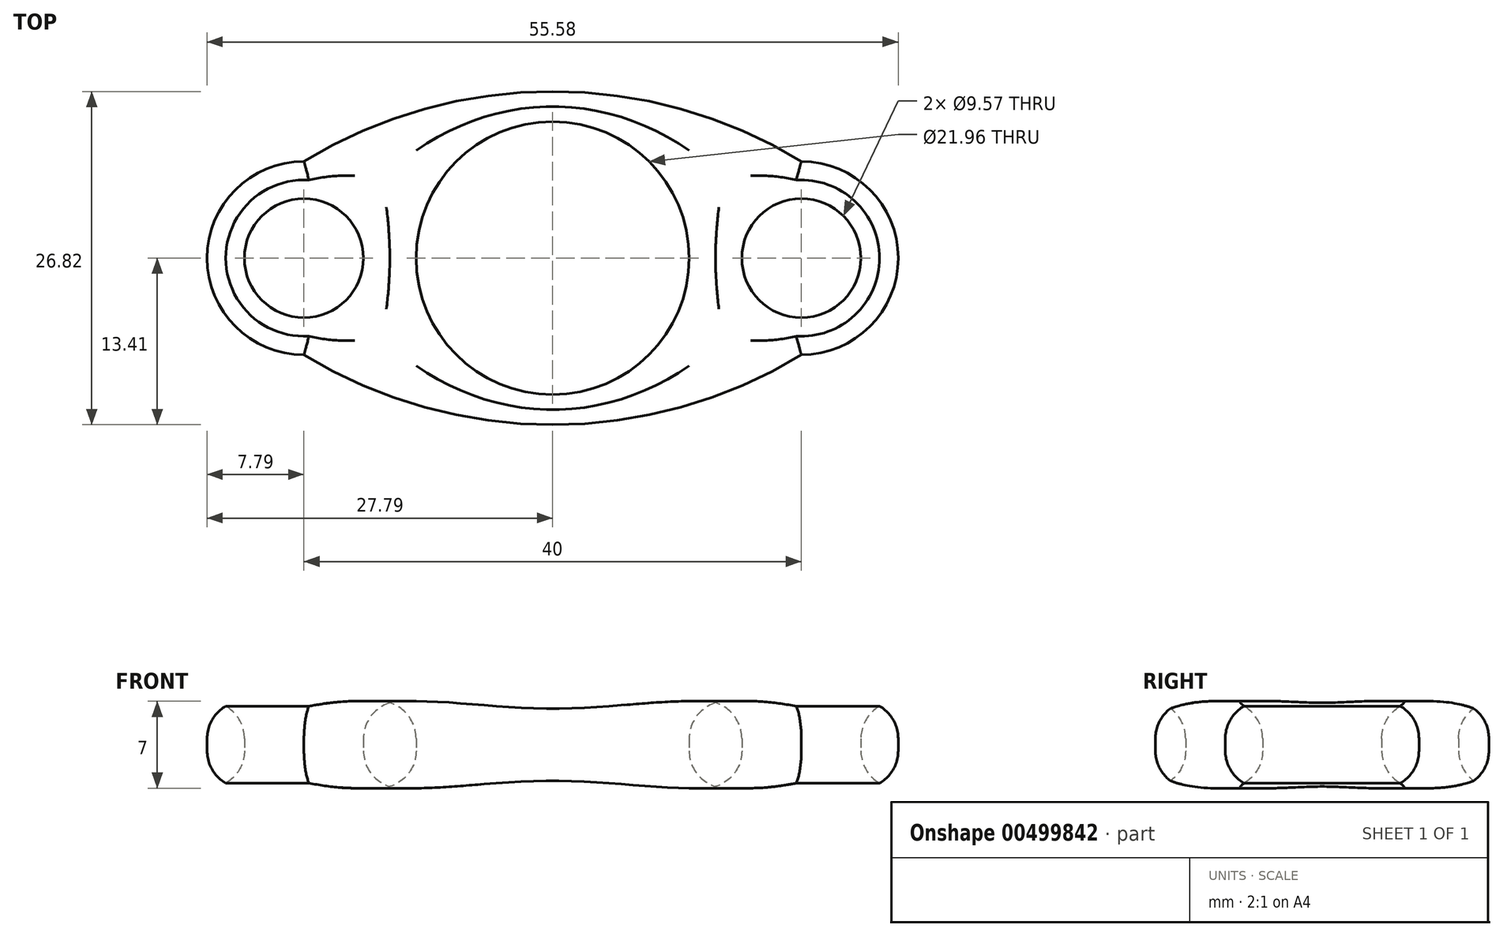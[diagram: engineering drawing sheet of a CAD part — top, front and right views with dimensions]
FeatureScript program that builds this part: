
annotation { "Feature Type Name" : "Feature", "Feature Type Description" : "" }
export const myFeature = defineFeature(function(context is Context, id is Id, definition is map)
    precondition{}
    {
        {
            var Q0;
            Q0=qCreatedBy(makeId("Top.planeOp"),FACE);
            var sketch = newSketch(context, id + "F0", { "sketchPlane" : qUnion([Q0])});
            skCircle(sketch, "E0", {"center": v(0, 0) * mm, "radius": 10.98 * mm});
            skCircle(sketch, "E1", {"center": v(-20, 0) * mm, "radius": 4.79 * mm});
            skCircle(sketch, "E2", {"center": v(20, 0) * mm, "radius": 4.79 * mm});
            skArc(sketch, "E3", {"start": v(-20, 7.79) * mm, "mid": v(-27.79, 0) * mm, "end": v(-20, -7.79) * mm});
            skArc(sketch, "E4", {"start": v(20, -7.79) * mm, "mid": v(27.79, 0) * mm, "end": v(20, 7.79) * mm});
            skArc(sketch, "E5", {"start": v(20, 7.79) * mm, "mid": v(0, 13.41) * mm, "end": v(-20, 7.79) * mm});
            skArc(sketch, "E6", {"start": v(-20, -7.79) * mm, "mid": v(0, -13.41) * mm, "end": v(20, -7.79) * mm});
            skPoint(sketch, "E7.orphan", {"position": v(0, 20) * mm});
            skPoint(sketch, "E8.trimOffspring.end.orphan", {"position": v(0, -20) * mm});
            skSolve(sketch);
        }
        {
            var Q0;
            Q0=makeQuery(id+"F0.imprint","IMPRINT",FACE,{"disambiguationData":[TD([[makeQuery(id+"F0.imprint","IMPRINT",EDGE,{"derivedFrom":sQuery(id+"F0.wireOp",EDGE,"t2C2Or2h-0svl-AiJ2-E9LP-vN88mKRXYnXd")}),-1.0]])]});
            var Q1;
            {var subQ0=sQuery(id+"F0.wireOp",EDGE,"wKvYZZdL-JQlj-ovzd-Wz5h-iNcVovLRUGSe");Q1=makeQuery(id+"F0.imprint","IMPRINT",FACE,{"disambiguationData":[TD([[makeQuery(id+"F0.imprint","IMPRINT",EDGE,{"derivedFrom":subQ0}),1.0]])]});}
            var Q2;
            Q2=makeQuery(id+"F0.imprint","IMPRINT",FACE,{"disambiguationData":[TD([[makeQuery(id+"F0.imprint","IMPRINT",EDGE,{"derivedFrom":sQuery(id+"F0.wireOp",EDGE,"E0")}),-1.0]])]});
            var Q3;
            {var subQ0=sQuery(id+"F0.wireOp",EDGE,"G6ESekOY-lkIH-LnHm-BnSb-OE4Pec71Upx1");Q3=makeQuery(id+"F0.imprint","IMPRINT",FACE,{"disambiguationData":[TD([[makeQuery(id+"F0.imprint","IMPRINT",EDGE,{"derivedFrom":subQ0}),1.0]])]});}
            var Q4;
            Q4=makeQuery(id+"F0.imprint","IMPRINT",FACE,{"disambiguationData":[TD([[makeQuery(id+"F0.imprint","IMPRINT",EDGE,{"derivedFrom":sQuery(id+"F0.wireOp",EDGE,"1yo7BWKv-qR4V-7lZo-C7g4-YwKMsMvaXa0q")}),-1.0]])]});
            extrude(context, id + "F1", {"entities" : qUnion([Q0, Q1, Q2, Q3, Q4]), "depth" : 7 * mm, "offsetDistance" : 25 * mm});
        }
        {
            var Q0;
            Q0=makeQuery(id+"F1.opExtrude","CAP_FACE",FACE,{"disambiguationData":[OSD([sQuery(id+"F0.wireOp",EDGE,"E0"),sQuery(id+"F0.wireOp",EDGE,"E1"),sQuery(id+"F0.wireOp",EDGE,"E2"),sQuery(id+"F0.wireOp",EDGE,"E3"),sQuery(id+"F0.wireOp",EDGE,"E4"),sQuery(id+"F0.wireOp",EDGE,"E5"),sQuery(id+"F0.wireOp",EDGE,"E6")])],"isStart":false});
            var Q1;
            Q1=makeQuery(id+"F1.opExtrude","CAP_FACE",FACE,{"disambiguationData":[OSD([sQuery(id+"F0.wireOp",EDGE,"E0"),sQuery(id+"F0.wireOp",EDGE,"E1"),sQuery(id+"F0.wireOp",EDGE,"E2"),sQuery(id+"F0.wireOp",EDGE,"E3"),sQuery(id+"F0.wireOp",EDGE,"E4"),sQuery(id+"F0.wireOp",EDGE,"E5"),sQuery(id+"F0.wireOp",EDGE,"E6")])],"isStart":true});
            fillet(context, id + "F2", {"entities" : qUnion([Q0, Q1]), "radius" : 3 * mm, "tangentPropagation" : true, "allowEdgeOverflow" : false});
        }
    });
